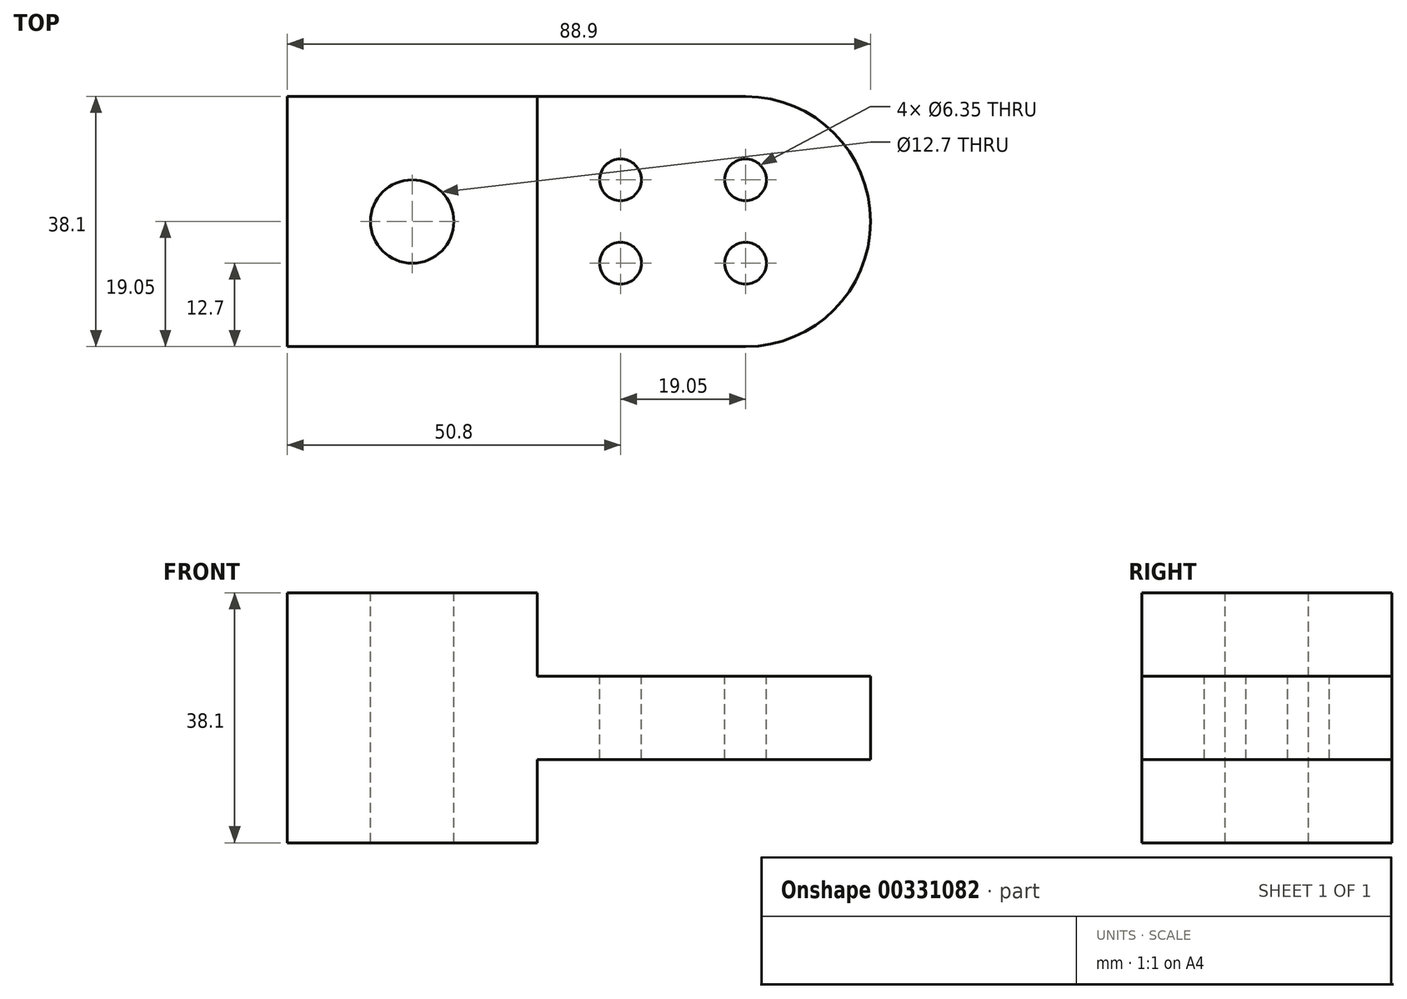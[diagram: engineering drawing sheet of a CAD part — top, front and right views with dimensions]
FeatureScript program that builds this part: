
annotation { "Feature Type Name" : "Feature", "Feature Type Description" : "" }
export const myFeature = defineFeature(function(context is Context, id is Id, definition is map)
    precondition{}
    {
        {
            var Q0;
            Q0=qCreatedBy(makeId("Top.planeOp"),FACE);
            var sketch = newSketch(context, id + "F0", { "sketchPlane" : qUnion([Q0])});
            skLineSegment(sketch, "E0.bottom", {"start": v(0, 0) * mm, "end": v(69.85, 0) * mm});
            skLineSegment(sketch, "E0.top", {"start": v(0, 38.1) * mm, "end": v(69.85, 38.1) * mm});
            skLineSegment(sketch, "E0.left", {"start": v(0, 0) * mm, "end": v(0, 38.1) * mm});
            skLineSegment(sketch, "E0.right", {"start": v(69.85, 0) * mm, "end": v(69.85, 38.1) * mm});
            skArc(sketch, "E1", {"start": v(69.85, 38.1) * mm, "mid": v(88.9, 19.05) * mm, "end": v(69.85, 0) * mm});
            skLineSegment(sketch, "E2", {"start": v(38.1, 38.1) * mm, "end": v(38.1, 0) * mm});
            skSolve(sketch);
        }
        {
            var Q0;
            {var subQ0=sQuery(id+"F0.wireOp",EDGE,"E0.left");Q0=makeQuery(id+"F0.imprint","IMPRINT",FACE,{"disambiguationData":[TD([[makeQuery(id+"F0.imprint","IMPRINT",EDGE,{"derivedFrom":subQ0}),-1.0]])]});}
            extrude(context, id + "F1", {"entities" : qUnion([Q0]), "endBound" : BoundingType.SYMMETRIC, "depth" : 38.1 * mm});
        }
        {
            var Q0;
            {var subQ1=sQuery(id+"F0.wireOp",EDGE,"E0.right");Q0=makeQuery(id+"F0.imprint","IMPRINT",FACE,{"disambiguationData":[TD([[makeQuery(id+"F0.imprint","IMPRINT",EDGE,{"derivedFrom":subQ1}),1.0]])]});}
            var Q1;
            Q1=makeQuery(id+"F0.imprint","IMPRINT",FACE,{"disambiguationData":[TD([[makeQuery(id+"F0.imprint","IMPRINT",EDGE,{"derivedFrom":sQuery(id+"F0.wireOp",EDGE,"E0.right")}),-1.0]])]});
            extrude(context, id + "F2", {"entities" : qUnion([Q0, Q1]), "operationType" : NewBodyOperationType.ADD, "endBound" : BoundingType.SYMMETRIC, "depth" : 12.7 * mm});
        }
        {
            var Q0;
            Q0=makeQuery(id+"F1.opExtrude","CAP_FACE",FACE,{"disambiguationData":[OSD([sQuery(id+"F0.wireOp",EDGE,"E0.bottom"),sQuery(id+"F0.wireOp",EDGE,"E0.top"),sQuery(id+"F0.wireOp",EDGE,"E0.left"),sQuery(id+"F0.wireOp",EDGE,"E2")])],"isStart":false});
            var sketch = newSketch(context, id + "F3", { "sketchPlane" : qUnion([Q0])});
            skCircle(sketch, "E3", {"center": v(19.05, 19.05) * mm, "radius": 6.35 * mm});
            skPoint(sketch, "E3.centerSnap0", {"position": v(0, 19.05) * mm});
            skLineSegment(sketch, "E4.bottom", {"start": v(69.85, 25.4) * mm, "end": v(50.8, 25.4) * mm, "construction": true});
            skLineSegment(sketch, "E4.top", {"start": v(69.85, 12.7) * mm, "end": v(50.8, 12.7) * mm, "construction": true});
            skLineSegment(sketch, "E4.left", {"start": v(69.85, 25.4) * mm, "end": v(69.85, 12.7) * mm, "construction": true});
            skLineSegment(sketch, "E4.right", {"start": v(50.8, 25.4) * mm, "end": v(50.8, 12.7) * mm, "construction": true});
            skCircle(sketch, "E5", {"center": v(50.8, 25.4) * mm, "radius": 3.18 * mm});
            skCircle(sketch, "E6", {"center": v(50.8, 12.7) * mm, "radius": 3.18 * mm});
            skCircle(sketch, "E7", {"center": v(69.85, 25.4) * mm, "radius": 3.18 * mm});
            skCircle(sketch, "E8", {"center": v(69.85, 12.7) * mm, "radius": 3.18 * mm});
            skSolve(sketch);
        }
        {
            var Q0;
            Q0 = qSketchRegion(id + "F3", true);
            extrude(context, id + "F4", {"entities" : qUnion([Q0]), "operationType" : NewBodyOperationType.REMOVE, "endBound" : BoundingType.THROUGH_ALL, "oppositeDirection" : true, "depth" : 25.4 * mm});
        }
    });
